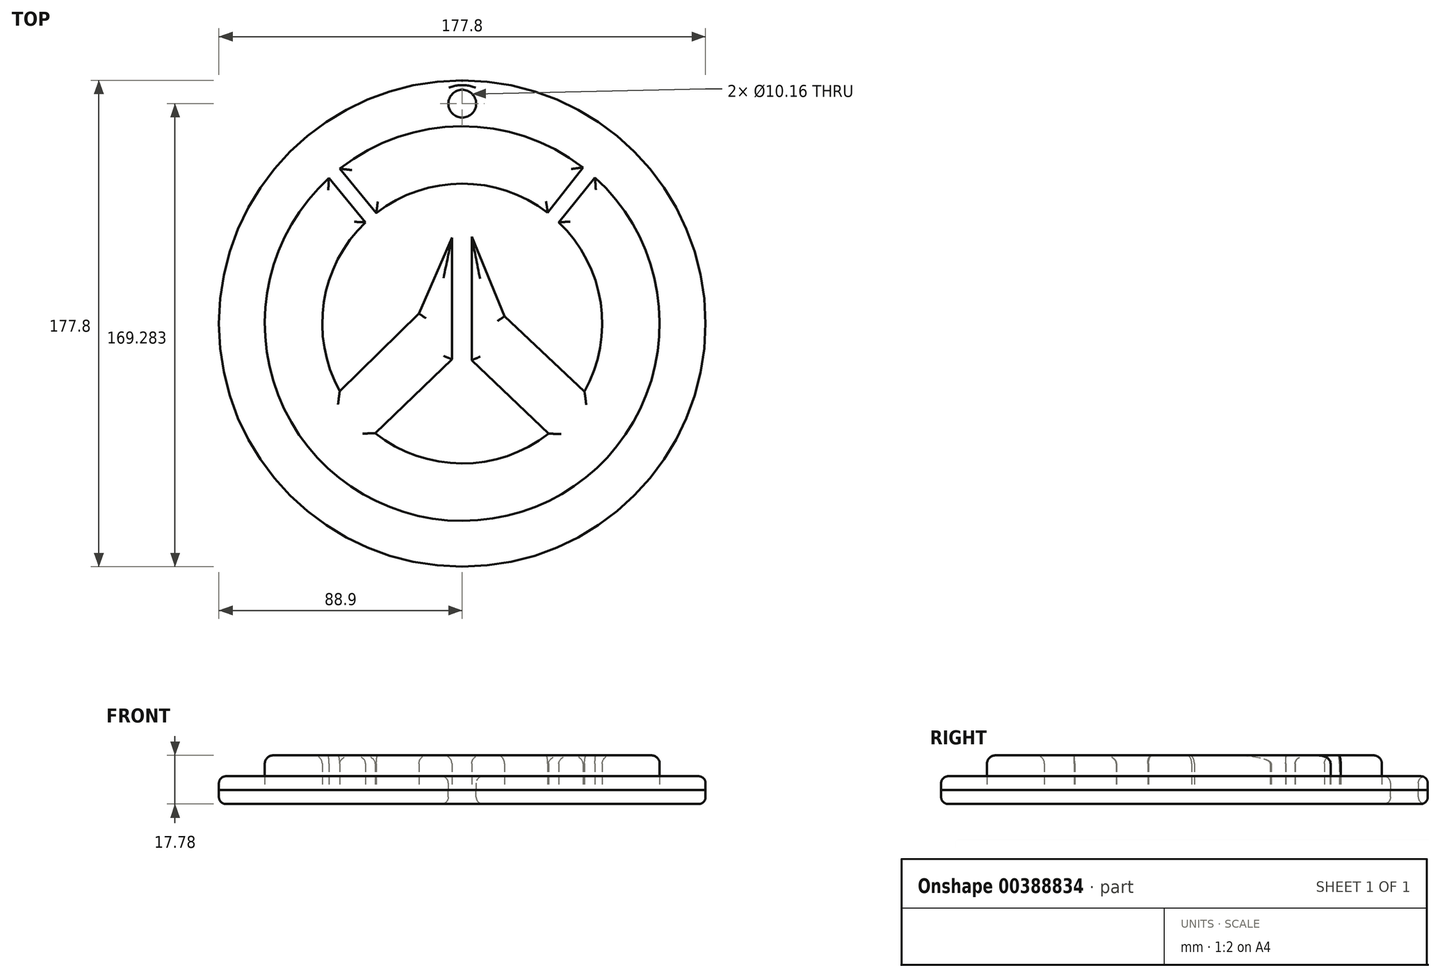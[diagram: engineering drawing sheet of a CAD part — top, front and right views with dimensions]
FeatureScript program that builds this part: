
annotation { "Feature Type Name" : "Feature", "Feature Type Description" : "" }
export const myFeature = defineFeature(function(context is Context, id is Id, definition is map)
    precondition{}
    {
        {
            var Q0;
            Q0=qCreatedBy(makeId("Top.planeOp"),FACE);
            var sketch = newSketch(context, id + "F0", { "sketchPlane" : qUnion([Q0])});
            skArc(sketch, "E0", {"start": v(-48.68, 53.24) * mm, "mid": v(0.12, -72.14) * mm, "end": v(48.51, 53.4) * mm});
            skArc(sketch, "E1", {"start": v(-35.32, 37) * mm, "mid": v(-50.56, 7.73) * mm, "end": v(-44.76, -24.75) * mm});
            skLineSegment(sketch, "E2", {"start": v(-48.68, 53.24) * mm, "end": v(-35.32, 37) * mm});
            skLineSegment(sketch, "E3", {"start": v(-44.72, 56.61) * mm, "end": v(-31.37, 40.4) * mm});
            skLineSegment(sketch, "E4", {"start": v(-44.76, -24.75) * mm, "end": v(-15.78, 3.63) * mm});
            skLineSegment(sketch, "E5", {"start": v(-15.78, 3.63) * mm, "end": v(-3.79, 31.4) * mm});
            skLineSegment(sketch, "E6", {"start": v(-3.79, 31.4) * mm, "end": v(-3.79, -13.1) * mm});
            skLineSegment(sketch, "E7", {"start": v(-3.79, -13.1) * mm, "end": v(-31.78, -40.08) * mm});
            skLineSegment(sketch, "E8", {"start": v(31.57, -40.25) * mm, "end": v(3.47, -13.41) * mm});
            skLineSegment(sketch, "E9", {"start": v(3.47, -13.41) * mm, "end": v(3.47, 31.72) * mm});
            skLineSegment(sketch, "E10", {"start": v(3.47, 31.72) * mm, "end": v(15.47, 2.68) * mm});
            skLineSegment(sketch, "E11", {"start": v(15.47, 2.68) * mm, "end": v(44.67, -24.91) * mm});
            skLineSegment(sketch, "E12", {"start": v(31.22, 40.52) * mm, "end": v(44.12, 57.08) * mm});
            skLineSegment(sketch, "E13", {"start": v(35.3, 37.02) * mm, "end": v(48.51, 53.4) * mm});
            skArc(sketch, "E14.trimOffspring", {"start": v(44.12, 57.08) * mm, "mid": v(-0.38, 72.14) * mm, "end": v(-44.72, 56.61) * mm});
            skArc(sketch, "E15.trimOffspring", {"start": v(31.22, 40.52) * mm, "mid": v(-0.1, 51.15) * mm, "end": v(-31.37, 40.4) * mm});
            skArc(sketch, "E16.trimOffspring", {"start": v(-31.78, -40.08) * mm, "mid": v(-0.13, -51.15) * mm, "end": v(31.57, -40.25) * mm});
            skArc(sketch, "E17.trimOffspring", {"start": v(44.67, -24.91) * mm, "mid": v(50.57, 7.66) * mm, "end": v(35.3, 37.02) * mm});
            skSolve(sketch);
        }
        {
            var Q0;
            Q0=qSketchRegion(id+"F0",true);
            extrude(context, id + "F1", {"entities" : qUnion([Q0]), "depth" : 12.7 * mm});
        }
        {
            var Q0;
            Q0=qCreatedBy(makeId("Top.planeOp"),FACE);
            var sketch = newSketch(context, id + "F2", { "sketchPlane" : qUnion([Q0])});
            skCircle(sketch, "E18", {"center": v(0, 0) * mm, "radius": 88.9 * mm});
            skCircle(sketch, "E19", {"center": v(0, 80.38) * mm, "radius": 5.08 * mm});
            skSolve(sketch);
        }
        {
            var Q0;
            Q0=makeQuery(id+"F1.opExtrude","CAP_FACE",FACE,{"disambiguationData":[OSD([sQuery(id+"F0.wireOp",EDGE,"E0"),sQuery(id+"F0.wireOp",EDGE,"E1"),sQuery(id+"F0.wireOp",EDGE,"E2"),sQuery(id+"F0.wireOp",EDGE,"E4"),sQuery(id+"F0.wireOp",EDGE,"E5"),sQuery(id+"F0.wireOp",EDGE,"E6"),sQuery(id+"F0.wireOp",EDGE,"E7"),sQuery(id+"F0.wireOp",EDGE,"E8"),sQuery(id+"F0.wireOp",EDGE,"E9"),sQuery(id+"F0.wireOp",EDGE,"E10"),sQuery(id+"F0.wireOp",EDGE,"E11"),sQuery(id+"F0.wireOp",EDGE,"E13"),sQuery(id+"F0.wireOp",EDGE,"E16.trimOffspring"),sQuery(id+"F0.wireOp",EDGE,"E17.trimOffspring")])],"isStart":false});
            var Q1;
            Q1=makeQuery(id+"F1.opExtrude","CAP_FACE",FACE,{"disambiguationData":[OSD([sQuery(id+"F0.wireOp",EDGE,"E3"),sQuery(id+"F0.wireOp",EDGE,"E12"),sQuery(id+"F0.wireOp",EDGE,"E14.trimOffspring"),sQuery(id+"F0.wireOp",EDGE,"E15.trimOffspring")])],"isStart":false});
            fillet(context, id + "F3", {"entities" : qUnion([Q0, Q1]), "radius" : 3.05 * mm, "tangentPropagation" : true, "allowEdgeOverflow" : false});
        }
        {
            var Q0;
            Q0=qSketchRegion(id+"F2",true);
            extrude(context, id + "F4", {"entities" : qUnion([Q0]), "depth" : 5.08 * mm});
        }
        {
            var Q0;
            Q0=makeQuery(id+"F4.opExtrude","CAP_FACE",FACE,{"disambiguationData":[OSD([sQuery(id+"F2.wireOp",EDGE,"E18"),sQuery(id+"F2.wireOp",EDGE,"E19")])],"isStart":false});
            fillet(context, id + "F5", {"entities" : qUnion([Q0]), "radius" : 2.54 * mm, "tangentPropagation" : true, "allowEdgeOverflow" : false});
        }
        {
            var Q0;
            Q0=makeQuery(id+"F4.opExtrude","CAP_FACE",FACE,{"disambiguationData":[OSD([sQuery(id+"F2.wireOp",EDGE,"E18"),sQuery(id+"F2.wireOp",EDGE,"E19")])],"isStart":true});
            extrude(context, id + "F6", {"entities" : qUnion([Q0]), "depth" : 5.08 * mm});
        }
        {
            var Q0;
            Q0=makeQuery(id+"F6.opExtrude","CAP_FACE",FACE,{"disambiguationData":[OSD([sQuery(id+"F2.wireOp",EDGE,"E18"),sQuery(id+"F2.wireOp",EDGE,"E19")])],"isStart":false});
            fillet(context, id + "F7", {"entities" : qUnion([Q0]), "radius" : 2.54 * mm, "tangentPropagation" : true, "allowEdgeOverflow" : false});
        }
    });
